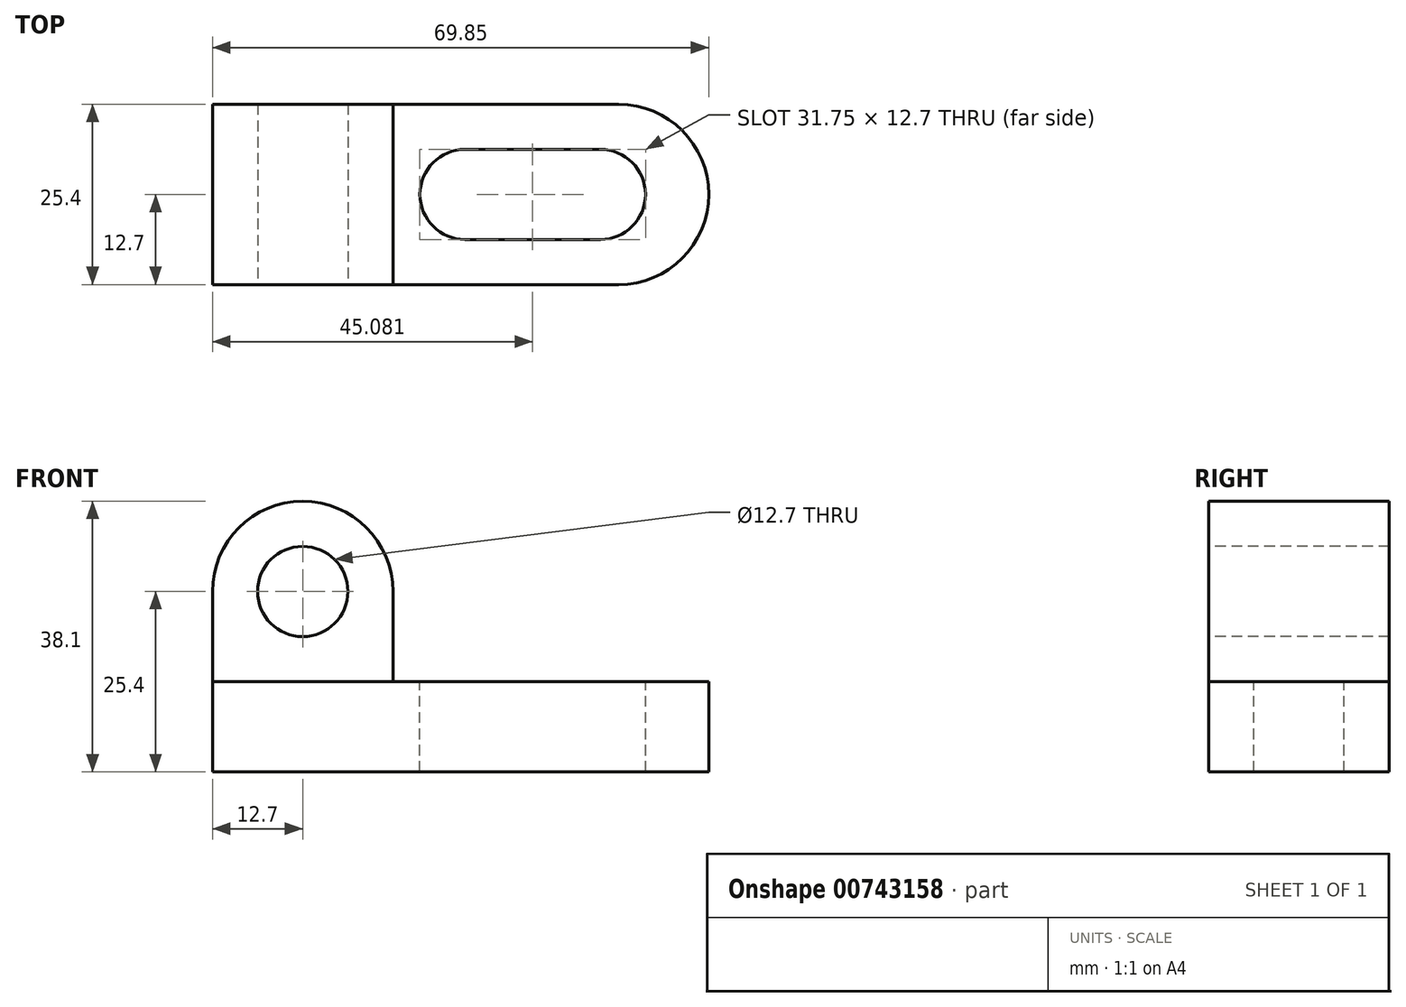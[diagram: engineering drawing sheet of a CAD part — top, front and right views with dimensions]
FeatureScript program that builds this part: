
annotation { "Feature Type Name" : "Feature", "Feature Type Description" : "" }
export const myFeature = defineFeature(function(context is Context, id is Id, definition is map)
    precondition{}
    {
        {
            var Q0;
            Q0=qCreatedBy(makeId("Top.planeOp"),FACE);
            var sketch = newSketch(context, id + "F0", { "sketchPlane" : qUnion([Q0])});
            skLineSegment(sketch, "E0", {"start": v(0, 0) * mm, "end": v(57.15, 0) * mm});
            skLineSegment(sketch, "E1", {"start": v(57.15, 0) * mm, "end": v(57.15, 25.4) * mm});
            skLineSegment(sketch, "E2", {"start": v(57.15, 25.4) * mm, "end": v(0, 25.4) * mm});
            skLineSegment(sketch, "E3", {"start": v(0, 25.4) * mm, "end": v(0, 0) * mm});
            skArc(sketch, "E4", {"start": v(57.15, 0) * mm, "mid": v(69.85, 12.7) * mm, "end": v(57.15, 25.4) * mm});
            skSolve(sketch);
        }
        {
            var Q0;
            Q0=makeQuery(id+"F0.imprint","IMPRINT",FACE,{"disambiguationData":[TD([[makeQuery(id+"F0.imprint","IMPRINT",EDGE,{"derivedFrom":sQuery(id+"F0.wireOp",EDGE,"E0")}),1.0]])]});
            extrude(context, id + "F1", {"entities" : qUnion([Q0]), "depth" : 12.7 * mm, "offsetDistance" : 25.4 * mm});
        }
        {
            var Q0;
            Q0 = qSketchRegion(id + "F0", true);
            extrude(context, id + "F2", {"entities" : qUnion([Q0]), "operationType" : NewBodyOperationType.ADD, "depth" : 12.7 * mm, "offsetDistance" : 25.4 * mm});
        }
        {
            var Q0;
            Q0=makeQuery(id+"F1.opExtrude","SWEPT_FACE",FACE,{"disambiguationData":[OSD([sQuery(id+"F0.wireOp",EDGE,"E0")])]});
            var sketch = newSketch(context, id + "F3", { "sketchPlane" : qUnion([Q0])});
            skLineSegment(sketch, "E5", {"start": v(0, 12.7) * mm, "end": v(0, 25.4) * mm});
            skLineSegment(sketch, "E6", {"start": v(0, 25.4) * mm, "end": v(25.4, 25.4) * mm});
            skLineSegment(sketch, "E7", {"start": v(25.4, 25.4) * mm, "end": v(25.4, 12.7) * mm});
            skLineSegment(sketch, "E8", {"start": v(25.4, 12.7) * mm, "end": v(0, 12.7) * mm});
            skArc(sketch, "E9", {"start": v(25.4, 25.4) * mm, "mid": v(12.7, 38.1) * mm, "end": v(0, 25.4) * mm});
            skSolve(sketch);
        }
        {
            var Q0;
            Q0 = qSketchRegion(id + "F3", true);
            extrude(context, id + "F4", {"entities" : qUnion([Q0]), "oppositeDirection" : true, "depth" : 25.4 * mm, "offsetDistance" : 25.4 * mm});
        }
        {
            var Q0;
            Q0=makeQuery(id+"F4.opExtrude","CAP_FACE",FACE,{"disambiguationData":[OSD([sQuery(id+"F3.wireOp",EDGE,"E5"),sQuery(id+"F3.wireOp",EDGE,"E7"),sQuery(id+"F3.wireOp",EDGE,"E8"),sQuery(id+"F3.wireOp",EDGE,"E9")])],"isStart":true});
            var sketch = newSketch(context, id + "F5", { "sketchPlane" : qUnion([Q0])});
            skCircle(sketch, "E10", {"center": v(12.7, 25.4) * mm, "radius": 6.35 * mm});
            skSolve(sketch);
        }
        {
            var Q0;
            Q0=makeQuery(id+"F5.imprint","IMPRINT",FACE,{"disambiguationData":[TD([[makeQuery(id+"F5.imprint","IMPRINT",EDGE,{"derivedFrom":sQuery(id+"F5.wireOp",EDGE,"E10")}),1.0]])]});
            extrude(context, id + "F6", {"entities" : qUnion([Q0]), "operationType" : NewBodyOperationType.REMOVE, "oppositeDirection" : true, "depth" : 25.4 * mm, "offsetDistance" : 25.4 * mm});
        }
        {
            var Q0;
            {var subQ0=sQuery(id+"F0.wireOp",EDGE,"E3");var subQ1=sQuery(id+"F0.wireOp",EDGE,"E2");var subQ2=sQuery(id+"F0.wireOp",EDGE,"E0");Q0=makeQuery(id+"F2.boolean.opBoolean","MERGE",FACE,{"derivedFrom":[makeQuery(id+"F1.opExtrude","CAP_FACE",FACE,{"disambiguationData":[OSD([subQ2,sQuery(id+"F0.wireOp",EDGE,"E1"),subQ1,subQ0])],"isStart":false}),makeQuery(id+"F2.opExtrude","CAP_FACE",FACE,{"disambiguationData":[OSD([subQ2,subQ1,subQ0,sQuery(id+"F0.wireOp",EDGE,"E4")])],"isStart":false})]});}
            var sketch = newSketch(context, id + "F7", { "sketchPlane" : qUnion([Q0])});
            skLineSegment(sketch, "E11", {"start": v(54.6, 19.05) * mm, "end": v(35.56, 19.05) * mm});
            skLineSegment(sketch, "E12", {"start": v(35.56, 19.05) * mm, "end": v(35.56, 6.35) * mm});
            skLineSegment(sketch, "E13", {"start": v(35.56, 6.35) * mm, "end": v(54.6, 6.35) * mm});
            skLineSegment(sketch, "E14", {"start": v(54.6, 6.35) * mm, "end": v(54.6, 19.05) * mm});
            skArc(sketch, "E15", {"start": v(54.6, 6.35) * mm, "mid": v(60.96, 12.7) * mm, "end": v(54.6, 19.05) * mm});
            skArc(sketch, "E16", {"start": v(35.56, 19.05) * mm, "mid": v(29.2, 12.7) * mm, "end": v(35.56, 6.35) * mm});
            skSolve(sketch);
        }
        {
            var Q0;
            Q0=makeQuery(id+"F7.imprint","IMPRINT",FACE,{"disambiguationData":[TD([[makeQuery(id+"F7.imprint","IMPRINT",EDGE,{"derivedFrom":sQuery(id+"F7.wireOp",EDGE,"E14")}),-1.0]])]});
            var Q1;
            Q1=makeQuery(id+"F7.imprint","IMPRINT",FACE,{"disambiguationData":[TD([[makeQuery(id+"F7.imprint","IMPRINT",EDGE,{"derivedFrom":sQuery(id+"F7.wireOp",EDGE,"E11")}),1.0]])]});
            var Q2;
            Q2=makeQuery(id+"F7.imprint","IMPRINT",FACE,{"disambiguationData":[TD([[makeQuery(id+"F7.imprint","IMPRINT",EDGE,{"derivedFrom":sQuery(id+"F7.wireOp",EDGE,"E12")}),-1.0]])]});
            extrude(context, id + "F8", {"entities" : qUnion([Q0, Q1, Q2]), "operationType" : NewBodyOperationType.REMOVE, "oppositeDirection" : true, "depth" : 25.4 * mm, "offsetDistance" : 25.4 * mm});
        }
    });
